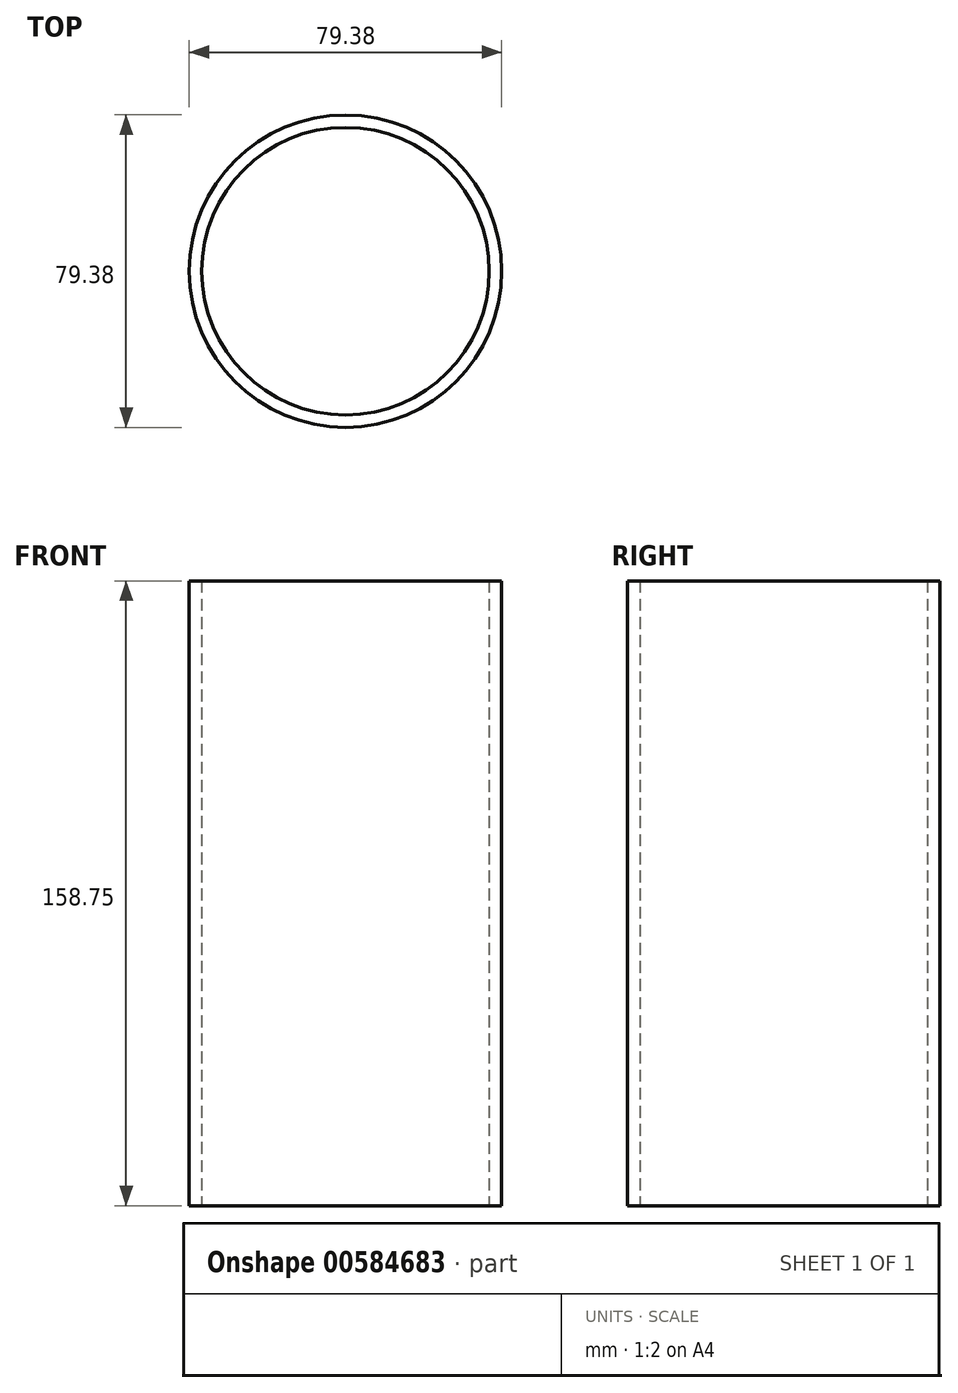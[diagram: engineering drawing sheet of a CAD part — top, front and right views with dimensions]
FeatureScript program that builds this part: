
annotation { "Feature Type Name" : "Feature", "Feature Type Description" : "" }
export const myFeature = defineFeature(function(context is Context, id is Id, definition is map)
    precondition{}
    {
        {
            var Q0;
            Q0=qCreatedBy(makeId("Top.planeOp"),FACE);
            var sketch = newSketch(context, id + "F0", { "sketchPlane" : qUnion([Q0])});
            skCircle(sketch, "E0", {"center": v(0, 0) * mm, "radius": 39.69 * mm});
            skCircle(sketch, "E1", {"center": v(0, 0) * mm, "radius": 36.51 * mm});
            skSolve(sketch);
        }
        {
            var Q0;
            Q0=makeQuery(id+"F0.imprint","IMPRINT",FACE,{"disambiguationData":[TD([[makeQuery(id+"F0.imprint","IMPRINT",EDGE,{"derivedFrom":sQuery(id+"F0.wireOp",EDGE,"E0")}),1.0]])]});
            extrude(context, id + "F1", {"entities" : qUnion([Q0]), "depth" : 158.75 * mm, "offsetDistance" : 25 * mm});
        }
    });
